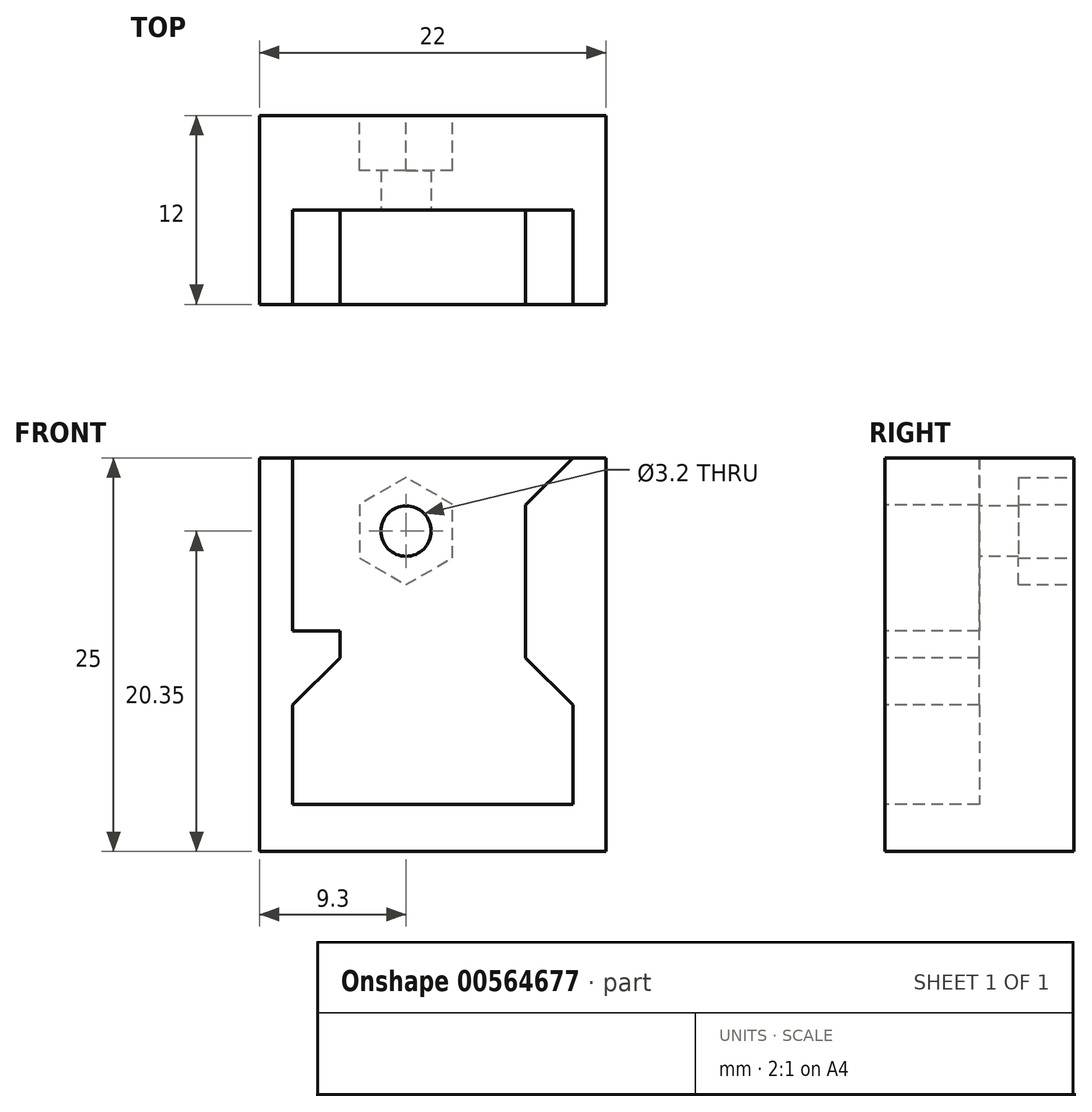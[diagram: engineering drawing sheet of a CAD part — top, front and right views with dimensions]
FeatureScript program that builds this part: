
annotation { "Feature Type Name" : "Feature", "Feature Type Description" : "" }
export const myFeature = defineFeature(function(context is Context, id is Id, definition is map)
    precondition{}
    {
        {
            var Q0;
            Q0=qCreatedBy(makeId("Front.planeOp"),FACE);
            var sketch = newSketch(context, id + "F0", { "sketchPlane" : qUnion([Q0])});
            skLineSegment(sketch, "E0.bottom", {"start": v(-11, 25) * mm, "end": v(11, 25) * mm});
            skLineSegment(sketch, "E0.top", {"start": v(-11, 0) * mm, "end": v(11, 0) * mm});
            skLineSegment(sketch, "E0.left", {"start": v(-11, 25) * mm, "end": v(-11, 0) * mm});
            skLineSegment(sketch, "E0.right", {"start": v(11, 25) * mm, "end": v(11, 0) * mm});
            skSolve(sketch);
        }
        {
            var Q0;
            Q0=makeQuery(id+"F0.imprint","IMPRINT",FACE,{"disambiguationData":[TD([[makeQuery(id+"F0.imprint","IMPRINT",EDGE,{"derivedFrom":sQuery(id+"F0.wireOp",EDGE,"E0.bottom")}),-1.0]])]});
            extrude(context, id + "F1", {"entities" : qUnion([Q0]), "oppositeDirection" : true, "depth" : 12 * mm});
        }
        {
            var Q0;
            Q0=makeQuery(id+"F1.opExtrude","CAP_FACE",FACE,{"disambiguationData":[OSD([sQuery(id+"F0.wireOp",EDGE,"E0.bottom"),sQuery(id+"F0.wireOp",EDGE,"E0.top"),sQuery(id+"F0.wireOp",EDGE,"E0.left"),sQuery(id+"F0.wireOp",EDGE,"E0.right")])],"isStart":true});
            var sketch = newSketch(context, id + "F2", { "sketchPlane" : qUnion([Q0])});
            skLineSegment(sketch, "E1.bottom", {"start": v(-8.9, 25) * mm, "end": v(8.9, 25) * mm});
            skLineSegment(sketch, "E1.top", {"start": v(-8.9, 3) * mm, "end": v(8.9, 3) * mm});
            skLineSegment(sketch, "E1.left", {"start": v(-8.9, 25) * mm, "end": v(-8.9, 3) * mm});
            skLineSegment(sketch, "E1.right", {"start": v(8.9, 25) * mm, "end": v(8.9, 3) * mm});
            skLineSegment(sketch, "E2", {"start": v(0, 25) * mm, "end": v(0, 0) * mm, "construction": true});
            skSolve(sketch);
        }
        {
            var Q0;
            Q0=makeQuery(id+"F2.imprint","IMPRINT",FACE,{"disambiguationData":[TD([[makeQuery(id+"F2.imprint","IMPRINT",EDGE,{"derivedFrom":sQuery(id+"F2.wireOp",EDGE,"E1.bottom")}),-1.0]])]});
            extrude(context, id + "F3", {"entities" : qUnion([Q0]), "operationType" : NewBodyOperationType.REMOVE, "oppositeDirection" : true, "depth" : 6 * mm});
        }
        {
            var Q0;
            Q0=makeQuery(id+"F1.opExtrude","CAP_FACE",FACE,{"disambiguationData":[OSD([sQuery(id+"F0.wireOp",EDGE,"E0.bottom"),sQuery(id+"F0.wireOp",EDGE,"E0.top"),sQuery(id+"F0.wireOp",EDGE,"E0.left"),sQuery(id+"F0.wireOp",EDGE,"E0.right")])],"isStart":true});
            var sketch = newSketch(context, id + "F4", { "sketchPlane" : qUnion([Q0])});
            skLineSegment(sketch, "E3", {"start": v(-8.9, 14) * mm, "end": v(-5.9, 14) * mm});
            skLineSegment(sketch, "E4", {"start": v(-5.9, 14) * mm, "end": v(-5.9, 12.3) * mm});
            skLineSegment(sketch, "E5", {"start": v(-5.9, 12.3) * mm, "end": v(-8.9, 9.3) * mm});
            skLineSegment(sketch, "E6", {"start": v(-8.9, 9.3) * mm, "end": v(-8.9, 14) * mm});
            skLineSegment(sketch, "E7", {"start": v(8.9, 25) * mm, "end": v(5.9, 22) * mm});
            skLineSegment(sketch, "E8", {"start": v(5.9, 22) * mm, "end": v(5.9, 12.3) * mm});
            skLineSegment(sketch, "E9", {"start": v(5.9, 12.3) * mm, "end": v(8.9, 9.3) * mm});
            skLineSegment(sketch, "E10", {"start": v(8.9, 9.3) * mm, "end": v(8.9, 25) * mm});
            skLineSegment(sketch, "E11", {"start": v(0, 0) * mm, "end": v(0, 23.04) * mm, "construction": true});
            skSolve(sketch);
        }
        {
            var Q0;
            Q0=makeQuery(id+"F4.imprint","IMPRINT",FACE,{"disambiguationData":[TD([[makeQuery(id+"F4.imprint","IMPRINT",EDGE,{"derivedFrom":sQuery(id+"F4.wireOp",EDGE,"E3")}),-1.0]])]});
            var Q1;
            Q1=makeQuery(id+"F4.imprint","IMPRINT",FACE,{"disambiguationData":[TD([[makeQuery(id+"F4.imprint","IMPRINT",EDGE,{"derivedFrom":sQuery(id+"F4.wireOp",EDGE,"E7")}),1.0]])]});
            var Q2;
            Q2=makeQuery(id+"F3.boolean.opBoolean","COPY",FACE,{"derivedFrom":makeQuery(id+"F3.opExtrude","CAP_FACE",FACE,{"disambiguationData":[OSD([sQuery(id+"F2.wireOp",EDGE,"E1.bottom"),sQuery(id+"F2.wireOp",EDGE,"E1.top"),sQuery(id+"F2.wireOp",EDGE,"E1.left"),sQuery(id+"F2.wireOp",EDGE,"E1.right")])],"isStart":false})});
            extrude(context, id + "F5", {"entities" : qUnion([Q0, Q1]), "operationType" : NewBodyOperationType.ADD, "endBound" : BoundingType.UP_TO_SURFACE, "oppositeDirection" : true, "endBoundEntityFace" : qUnion([Q2]), "depth" : 25 * mm});
        }
        {
            var Q0;
            Q0=makeQuery(id+"F3.boolean.opBoolean","COPY",FACE,{"derivedFrom":makeQuery(id+"F3.opExtrude","CAP_FACE",FACE,{"disambiguationData":[OSD([sQuery(id+"F2.wireOp",EDGE,"E1.bottom"),sQuery(id+"F2.wireOp",EDGE,"E1.top"),sQuery(id+"F2.wireOp",EDGE,"E1.left"),sQuery(id+"F2.wireOp",EDGE,"E1.right")])],"isStart":false})});
            var sketch = newSketch(context, id + "F6", { "sketchPlane" : qUnion([Q0])});
            skCircle(sketch, "E12", {"center": v(-1.7, 20.35) * mm, "radius": 1.6 * mm});
            skSolve(sketch);
        }
        {
            var Q0;
            Q0=makeQuery(id+"F6.imprint","IMPRINT",FACE,{"disambiguationData":[TD([[makeQuery(id+"F6.imprint","IMPRINT",EDGE,{"derivedFrom":sQuery(id+"F6.wireOp",EDGE,"E12")}),1.0]])]});
            extrude(context, id + "F7", {"entities" : qUnion([Q0]), "operationType" : NewBodyOperationType.REMOVE, "endBound" : BoundingType.THROUGH_ALL, "oppositeDirection" : true, "depth" : 25 * mm});
        }
        {
            var Q0;
            Q0=makeQuery(id+"F1.opExtrude","CAP_FACE",FACE,{"disambiguationData":[OSD([sQuery(id+"F0.wireOp",EDGE,"E0.bottom"),sQuery(id+"F0.wireOp",EDGE,"E0.top"),sQuery(id+"F0.wireOp",EDGE,"E0.left"),sQuery(id+"F0.wireOp",EDGE,"E0.right")])],"isStart":false});
            var sketch = newSketch(context, id + "F8", { "sketchPlane" : qUnion([Q0])});
            skCircle(sketch, "E13.cCircle", {"center": v(1.7, 20.35) * mm, "radius": 2.95 * mm, "construction": true});
            skLineSegment(sketch, "E13.0", {"start": v(4.65, 22.05) * mm, "end": v(4.65, 18.65) * mm});
            skLineSegment(sketch, "E13.1", {"start": v(4.65, 18.65) * mm, "end": v(1.7, 16.94) * mm});
            skLineSegment(sketch, "E13.2", {"start": v(1.7, 16.94) * mm, "end": v(-1.25, 18.65) * mm});
            skLineSegment(sketch, "E13.3", {"start": v(-1.25, 18.65) * mm, "end": v(-1.25, 22.05) * mm});
            skLineSegment(sketch, "E13.4", {"start": v(-1.25, 22.05) * mm, "end": v(1.7, 23.76) * mm});
            skLineSegment(sketch, "E13.5", {"start": v(1.7, 23.76) * mm, "end": v(4.65, 22.05) * mm});
            skPoint(sketch, "E13.0.midPoint", {"position": v(4.65, 20.35) * mm});
            skSolve(sketch);
        }
        {
            var Q0;
            Q0=qSketchRegion(id+"F8",true);
            extrude(context, id + "F9", {"entities" : qUnion([Q0]), "operationType" : NewBodyOperationType.REMOVE, "oppositeDirection" : true, "depth" : 3.5 * mm});
        }
    });
